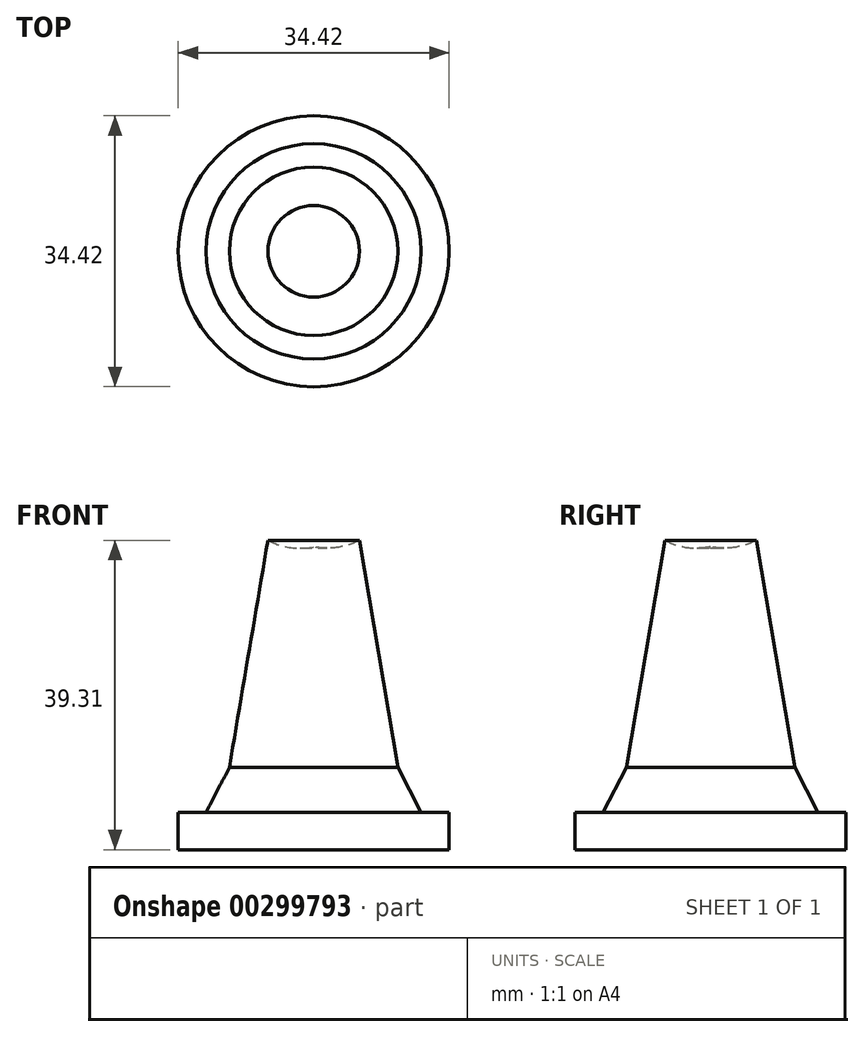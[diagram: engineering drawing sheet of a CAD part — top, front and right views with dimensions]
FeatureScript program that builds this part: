
annotation { "Feature Type Name" : "Feature", "Feature Type Description" : "" }
export const myFeature = defineFeature(function(context is Context, id is Id, definition is map)
    precondition{}
    {
        {
            var Q0;
            Q0=qCreatedBy(makeId("Front.planeOp"),FACE);
            var sketch = newSketch(context, id + "F0", { "sketchPlane" : qUnion([Q0])});
            skLineSegment(sketch, "E0", {"start": v(0, 0) * mm, "end": v(0, 55.82) * mm});
            skArc(sketch, "E1", {"start": v(0, 55.82) * mm, "mid": v(-10.06, 50.08) * mm, "end": v(-5.81, 39.3) * mm});
            skLineSegment(sketch, "E2", {"start": v(-5.81, 39.3) * mm, "end": v(-10.7, 10.47) * mm});
            skLineSegment(sketch, "E3", {"start": v(-10.7, 10.47) * mm, "end": v(-13.67, 4.72) * mm});
            skLineSegment(sketch, "E4", {"start": v(-13.67, 4.72) * mm, "end": v(-17.21, 4.72) * mm});
            skLineSegment(sketch, "E5", {"start": v(-17.21, 4.72) * mm, "end": v(-17.21, 0) * mm});
            skLineSegment(sketch, "E6", {"start": v(-17.21, 0) * mm, "end": v(0, 0) * mm});
            skSolve(sketch);
        }
        {
            var Q0;
            Q0=makeQuery(id+"F0.imprint","IMPRINT",FACE,{"disambiguationData":[TD([[makeQuery(id+"F0.imprint","IMPRINT",EDGE,{"derivedFrom":sQuery(id+"F0.wireOp",EDGE,"E0")}),1.0]])]});
            var Q1;
            Q1=sQuery(id+"F0.wireOp",EDGE,"E0");
            revolve(context, id + "F1", {"entities" : qUnion([Q0]), "axis" : qUnion([Q1]), "revolveType" : RevolveType.FULL});
        }
    });
